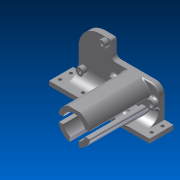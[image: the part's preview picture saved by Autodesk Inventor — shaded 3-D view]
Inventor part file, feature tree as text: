
AUTODESK INVENTOR PART (.ipt)
format: ipt  version: 2012 (Build 160160000, 160)  size: 390,656 bytes
history: native  units: in
note: dims shown in document units (in); Inventor stores cm internally (conversion verified against a paired STEP export)
features: fillet x1, other x1, imported_body x1
ambient origin geometry x8: Origin, YZ Plane, XZ Plane, XY Plane, X Axis, Y Axis, Z Axis, Center Point
feature tree (3):
  fillet  "Fillet15"  [1 undecoded]
  other  "Lanzamiento LP v51"
  imported_body  "Base1"
note: 1 required parameter value undecoded (feature->parameter linkage not recoverable at this tier; creation-order binding heuristic only, values carry confidence <= 0.55)
